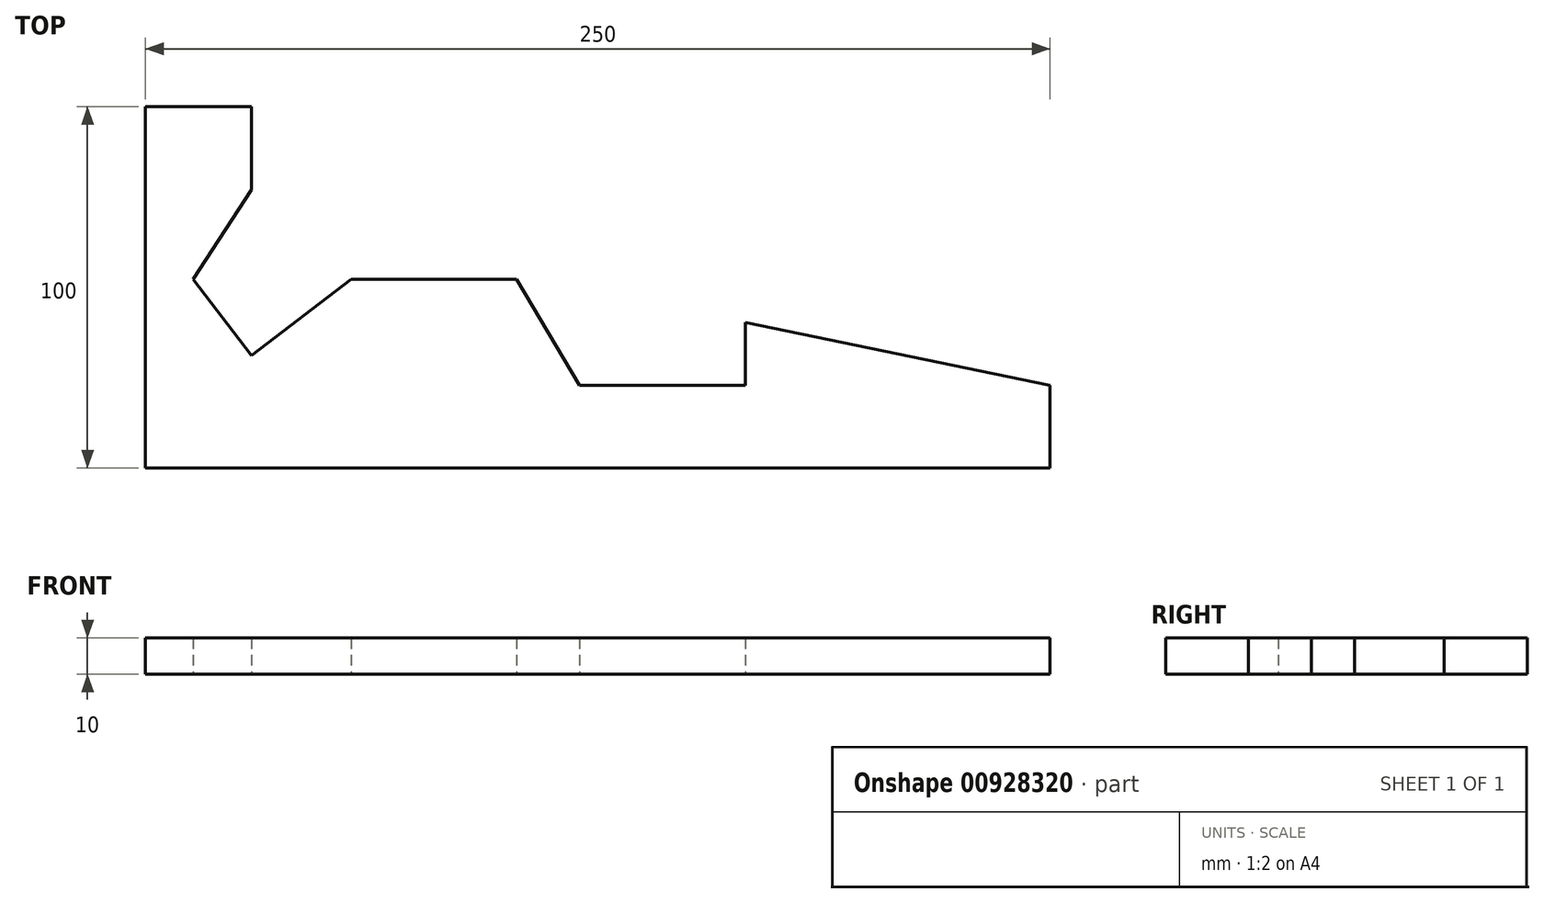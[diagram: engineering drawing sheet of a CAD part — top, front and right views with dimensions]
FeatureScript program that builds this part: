
annotation { "Feature Type Name" : "Feature", "Feature Type Description" : "" }
export const myFeature = defineFeature(function(context is Context, id is Id, definition is map)
    precondition{}
    {
        {
            var Q0;
            Q0=qCreatedBy(makeId("Top.planeOp"),FACE);
            var sketch = newSketch(context, id + "F0", { "sketchPlane" : qUnion([Q0])});
            skLineSegment(sketch, "E0", {"start": v(-275.68, -4.91) * mm, "end": v(-25.68, -4.91) * mm});
            skLineSegment(sketch, "E1", {"start": v(-275.68, -4.91) * mm, "end": v(-275.68, 95.09) * mm});
            skLineSegment(sketch, "E2", {"start": v(-25.68, -4.91) * mm, "end": v(-25.68, 18) * mm});
            skLineSegment(sketch, "E3", {"start": v(-25.68, 18) * mm, "end": v(-109.92, 35.4) * mm});
            skLineSegment(sketch, "E4", {"start": v(-109.92, 35.4) * mm, "end": v(-109.92, 18) * mm});
            skLineSegment(sketch, "E5", {"start": v(-109.92, 18) * mm, "end": v(-155.7, 18) * mm});
            skLineSegment(sketch, "E6", {"start": v(-155.7, 18) * mm, "end": v(-173.1, 47.3) * mm});
            skLineSegment(sketch, "E7", {"start": v(-173.1, 47.3) * mm, "end": v(-218.9, 47.3) * mm});
            skLineSegment(sketch, "E8", {"start": v(-218.9, 47.3) * mm, "end": v(-246.36, 26.23) * mm});
            skLineSegment(sketch, "E9", {"start": v(-246.36, 26.23) * mm, "end": v(-262.5, 47.3) * mm});
            skLineSegment(sketch, "E10", {"start": v(-262.5, 47.3) * mm, "end": v(-246.36, 72.02) * mm});
            skLineSegment(sketch, "E11", {"start": v(-246.36, 72.02) * mm, "end": v(-246.36, 95.09) * mm});
            skLineSegment(sketch, "E12", {"start": v(-246.36, 95.09) * mm, "end": v(-275.68, 95.09) * mm});
            skSolve(sketch);
        }
        {
            var Q0;
            Q0 = qSketchRegion(id + "F0", true);
            extrude(context, id + "F1", {"entities" : qUnion([Q0]), "depth" : 10 * mm, "offsetDistance" : 25 * mm});
        }
    });
